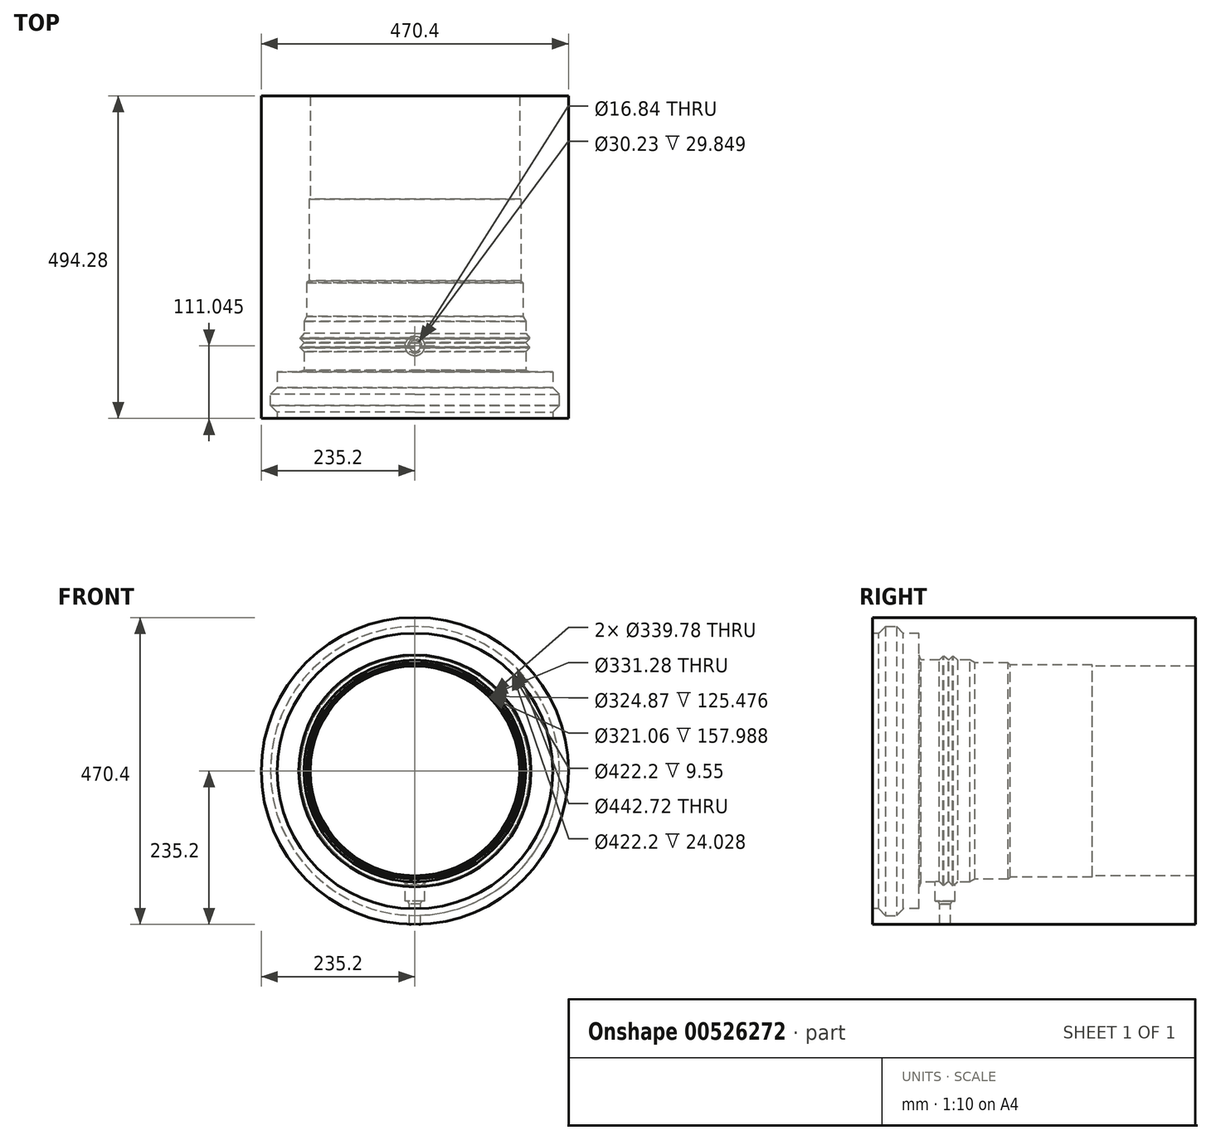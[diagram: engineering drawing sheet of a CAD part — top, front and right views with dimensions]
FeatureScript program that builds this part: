
annotation { "Feature Type Name" : "Feature", "Feature Type Description" : "" }
export const myFeature = defineFeature(function(context is Context, id is Id, definition is map)
    precondition{}
    {
        {
            var Q0;
            Q0=qCreatedBy(makeId("Front.planeOp"),FACE);
            var sketch = newSketch(context, id + "F0", { "sketchPlane" : qUnion([Q0])});
            skCircle(sketch, "E0", {"center": v(0, 0) * mm, "radius": 235.2 * mm});
            skSolve(sketch);
        }
        {
            var Q0;
            Q0 = qSketchRegion(id + "F0", true);
            extrude(context, id + "F1", {"entities" : qUnion([Q0]), "depth" : 494.28 * mm, "offsetDistance" : 25.4 * mm});
        }
        {
            var Q0;
            Q0=makeQuery(id+"F1.opExtrude","CAP_FACE",FACE,{"disambiguationData":[OSD([sQuery(id+"F0.wireOp",EDGE,"E0")])],"isStart":false});
            var sketch = newSketch(context, id + "F2", { "sketchPlane" : qUnion([Q0])});
            skCircle(sketch, "E1", {"center": v(0, 0) * mm, "radius": 160.53 * mm});
            skSolve(sketch);
        }
        {
            var Q0;
            Q0 = qSketchRegion(id + "F2", true);
            var Q1;
            Q1=makeQuery(id+"F2.imprint","IMPRINT",FACE,{"disambiguationData":[TD([[makeQuery(id+"F2.imprint","IMPRINT",EDGE,{"derivedFrom":sQuery(id+"F2.wireOp",EDGE,"E1")}),1.0]])]});
            extrude(context, id + "F3", {"entities" : qUnion([Q0, Q1]), "operationType" : NewBodyOperationType.REMOVE, "oppositeDirection" : true, "depth" : 947.42 * mm, "offsetDistance" : 25.4 * mm});
        }
        {
            var Q0;
            Q0=makeQuery(id+"F1.opExtrude","CAP_FACE",FACE,{"disambiguationData":[OSD([sQuery(id+"F0.wireOp",EDGE,"E0")])],"isStart":false});
            var sketch = newSketch(context, id + "F4", { "sketchPlane" : qUnion([Q0])});
            skCircle(sketch, "E2", {"center": v(0, 0) * mm, "radius": 162.43 * mm});
            skCircle(sketch, "E3", {"center": v(0, 0) * mm, "radius": 139.01 * mm});
            skSolve(sketch);
        }
        {
            var Q0;
            Q0 = qSketchRegion(id + "F4", true);
            extrude(context, id + "F5", {"entities" : qUnion([Q0]), "operationType" : NewBodyOperationType.REMOVE, "oppositeDirection" : true, "depth" : 336.3 * mm, "offsetDistance" : 25.4 * mm});
        }
        {
            var Q0;
            Q0=makeQuery(id+"F1.opExtrude","CAP_FACE",FACE,{"disambiguationData":[OSD([sQuery(id+"F0.wireOp",EDGE,"E0")])],"isStart":false});
            var sketch = newSketch(context, id + "F6", { "sketchPlane" : qUnion([Q0])});
            skCircle(sketch, "E4", {"center": v(0, 0) * mm, "radius": 165.64 * mm});
            skCircle(sketch, "E5", {"center": v(0, 0) * mm, "radius": 130.06 * mm});
            skSolve(sketch);
        }
        {
            var Q0;
            Q0 = qSketchRegion(id + "F6", true);
            extrude(context, id + "F7", {"entities" : qUnion([Q0]), "operationType" : NewBodyOperationType.REMOVE, "oppositeDirection" : true, "depth" : 205.74 * mm, "offsetDistance" : 25.4 * mm});
        }
        {
            var Q0;
            Q0=makeQuery(id+"F7.boolean.opBoolean","INTERSECT",EDGE,{"derivedFrom":[makeQuery(id+"F5.boolean.opBoolean","COPY",FACE,{"derivedFrom":makeQuery(id+"F5.opExtrude","SWEPT_FACE",FACE,{"disambiguationData":[OSD([sQuery(id+"F4.wireOp",EDGE,"E2")])]})}),makeQuery(id+"F7.opExtrude","CAP_FACE",FACE,{"disambiguationData":[OSD([sQuery(id+"F6.wireOp",EDGE,"E4"),sQuery(id+"F6.wireOp",EDGE,"E5")])],"isStart":false})]});
            chamfer(context, id + "F8", {"entities" : qUnion([Q0]), "width" : 5.08 * mm, "tangentPropagation" : true});
        }
        {
            var Q0;
            Q0=makeQuery(id+"F1.opExtrude","CAP_FACE",FACE,{"disambiguationData":[OSD([sQuery(id+"F0.wireOp",EDGE,"E0")])],"isStart":false});
            var sketch = newSketch(context, id + "F9", { "sketchPlane" : qUnion([Q0])});
            skCircle(sketch, "E6", {"center": v(0, 0) * mm, "radius": 169.89 * mm});
            skCircle(sketch, "E7", {"center": v(0, 0) * mm, "radius": 9.4 * mm});
            skSolve(sketch);
        }
        {
            var Q0;
            Q0 = qSketchRegion(id + "F9", true);
            extrude(context, id + "F10", {"entities" : qUnion([Q0]), "operationType" : NewBodyOperationType.REMOVE, "oppositeDirection" : true, "depth" : 147.57 * mm, "offsetDistance" : 25.4 * mm});
        }
        {
            var Q0;
            Q0=makeQuery(id+"F10.boolean.opBoolean","INTERSECT",EDGE,{"derivedFrom":[makeQuery(id+"F7.boolean.opBoolean","COPY",FACE,{"derivedFrom":makeQuery(id+"F7.opExtrude","SWEPT_FACE",FACE,{"disambiguationData":[OSD([sQuery(id+"F6.wireOp",EDGE,"E4")])]})}),makeQuery(id+"F10.opExtrude","CAP_FACE",FACE,{"disambiguationData":[OSD([sQuery(id+"F9.wireOp",EDGE,"E6"),sQuery(id+"F9.wireOp",EDGE,"E7")])],"isStart":false})]});
            chamfer(context, id + "F11", {"entities" : qUnion([Q0]), "chamferType" : ChamferType.OFFSET_ANGLE, "width" : 5.08 * mm, "oppositeDirection" : false, "angle" : 60 * degree, "tangentPropagation" : true});
        }
        {
            var Q0;
            Q0=makeQuery(id+"F1.opExtrude","CAP_FACE",FACE,{"disambiguationData":[OSD([sQuery(id+"F0.wireOp",EDGE,"E0")])],"isStart":false});
            var sketch = newSketch(context, id + "F12", { "sketchPlane" : qUnion([Q0])});
            skCircle(sketch, "E8", {"center": v(0, 0) * mm, "radius": 211.1 * mm});
            skCircle(sketch, "E9", {"center": v(0, 0) * mm, "radius": 37.7 * mm});
            skSolve(sketch);
        }
        {
            var Q0;
            Q0 = qSketchRegion(id + "F12", true);
            extrude(context, id + "F13", {"entities" : qUnion([Q0]), "operationType" : NewBodyOperationType.REMOVE, "oppositeDirection" : true, "depth" : 71.12 * mm, "offsetDistance" : 25.4 * mm});
        }
        {
            var Q0;
            Q0=qCreatedBy(makeId("Right.planeOp"),FACE);
            var sketch = newSketch(context, id + "F14", { "sketchPlane" : qUnion([Q0])});
            skPoint(sketch, "E10", {"position": v(-423.16, -177.8) * mm});
            skLineSegment(sketch, "E11", {"start": v(0, 0) * mm, "end": v(-511.48, 0) * mm});
            skLineSegment(sketch, "E12", {"start": v(-423.16, -177.8) * mm, "end": v(-415.34, -156.3) * mm});
            skLineSegment(sketch, "E13", {"start": v(-415.34, -156.3) * mm, "end": v(-438.26, -160.36) * mm});
            skLineSegment(sketch, "E14", {"start": v(-438.26, -160.36) * mm, "end": v(-423.16, -177.8) * mm});
            skPoint(sketch, "E15", {"position": v(-474.47, -221.36) * mm});
            skLineSegment(sketch, "E16", {"start": v(-474.47, -221.36) * mm, "end": v(-457.45, -221.36) * mm});
            skLineSegment(sketch, "E17", {"start": v(-457.45, -221.36) * mm, "end": v(-444.69, -208.6) * mm});
            skLineSegment(sketch, "E18", {"start": v(-474.47, -221.36) * mm, "end": v(-489.41, -206.42) * mm});
            skLineSegment(sketch, "E19", {"start": v(-489.41, -206.42) * mm, "end": v(-444.69, -208.6) * mm});
            skSolve(sketch);
        }
        {
            var Q0;
            Q0 = qSketchRegion(id + "F14", true);
            var Q1;
            Q1=sQuery(id+"F14.wireOp",EDGE,"E11");
            revolve(context, id + "F15", {"operationType" : NewBodyOperationType.REMOVE, "entities" : qUnion([Q0]), "axis" : qUnion([Q1]), "revolveType" : RevolveType.FULL});
        }
        {
            var Q0;
            Q0=qCreatedBy(makeId("Top.planeOp"),FACE);
            var sketch = newSketch(context, id + "F16", { "sketchPlane" : qUnion([Q0])});
            skLineSegment(sketch, "E20", {"start": v(0, -501.61) * mm, "end": v(0, -486.78) * mm});
            skPoint(sketch, "E21", {"position": v(169.89, -392.1) * mm});
            skLineSegment(sketch, "E22", {"start": v(175.64, -386.35) * mm, "end": v(175.64, -385.14) * mm});
            skLineSegment(sketch, "E23", {"start": v(169.89, -392.1) * mm, "end": v(175.64, -386.35) * mm});
            skLineSegment(sketch, "E24", {"start": v(169.89, -378.28) * mm, "end": v(169.89, -377.77) * mm});
            skLineSegment(sketch, "E25", {"start": v(169.89, -377.77) * mm, "end": v(175.64, -372.02) * mm});
            skPoint(sketch, "E26", {"position": v(169.89, -378.28) * mm});
            skLineSegment(sketch, "E27", {"start": v(169.89, -378.28) * mm, "end": v(175.7, -385.2) * mm});
            skLineSegment(sketch, "E28.trimOffspring", {"start": v(175.64, -372.02) * mm, "end": v(175.64, -370.84) * mm});
            skPoint(sketch, "E29.start.orphan", {"position": v(169.89, -362.9) * mm});
            skLineSegment(sketch, "E30", {"start": v(169.89, -363.98) * mm, "end": v(175.64, -370.84) * mm});
            skLineSegment(sketch, "E31", {"start": v(169.89, -392.1) * mm, "end": v(164, -392.1) * mm});
            skLineSegment(sketch, "E32", {"start": v(164, -392.1) * mm, "end": v(164, -363.98) * mm});
            skLineSegment(sketch, "E33", {"start": v(164, -363.98) * mm, "end": v(169.89, -363.98) * mm});
            skSolve(sketch);
        }
        {
            var Q0;
            Q0 = qSketchRegion(id + "F16", true);
            var Q1;
            Q1=sQuery(id+"F16.wireOp",EDGE,"E20");
            revolve(context, id + "F17", {"operationType" : NewBodyOperationType.REMOVE, "entities" : qUnion([Q0]), "axis" : qUnion([Q1]), "revolveType" : RevolveType.FULL, "oppositeDirection" : true});
        }
        {
            var Q0;
            Q0=qCreatedBy(makeId("Top.planeOp"),FACE);
            cPlane(context, id + "F18", {"entities" : qUnion([Q0]), "cplaneType" : CPlaneType.OFFSET, "offset" : 164.6 * mm, "oppositeDirection" : true, "width" : 152.4 * mm, "height" : 152.4 * mm});
        }
        {
            var Q0;
            Q0=qCreatedBy(id+"F18.planeOp",FACE);
            var sketch = newSketch(context, id + "F19", { "sketchPlane" : qUnion([Q0])});
            skCircle(sketch, "E34", {"center": v(0, -383.24) * mm, "radius": 8.42 * mm});
            skSolve(sketch);
        }
        {
            var Q0;
            Q0 = qSketchRegion(id + "F19", true);
            extrude(context, id + "F20", {"entities" : qUnion([Q0]), "operationType" : NewBodyOperationType.REMOVE, "oppositeDirection" : true, "depth" : 76.2 * mm, "offsetDistance" : 25.4 * mm});
        }
        {
            var Q0;
            Q0=qCreatedBy(id+"F18.planeOp",FACE);
            var sketch = newSketch(context, id + "F21", { "sketchPlane" : qUnion([Q0])});
            skCircle(sketch, "E35", {"center": v(0, -383.24) * mm, "radius": 15.11 * mm});
            skSolve(sketch);
        }
        {
            var Q0;
            Q0 = qSketchRegion(id + "F21", true);
            extrude(context, id + "F22", {"entities" : qUnion([Q0]), "operationType" : NewBodyOperationType.REMOVE, "oppositeDirection" : true, "depth" : 34.54 * mm, "offsetDistance" : 25.4 * mm});
        }
        {
            var Q0;
            Q0=makeQuery(id+"F22.boolean.opBoolean","INTERSECT",EDGE,{"derivedFrom":[makeQuery(id+"F20.boolean.opBoolean","COPY",FACE,{"derivedFrom":makeQuery(id+"F20.opExtrude","SWEPT_FACE",FACE,{"disambiguationData":[OSD([sQuery(id+"F19.wireOp",EDGE,"E34")])]})}),makeQuery(id+"F22.opExtrude","CAP_FACE",FACE,{"disambiguationData":[OSD([sQuery(id+"F21.wireOp",EDGE,"E35")])],"isStart":false})]});
            chamfer(context, id + "F23", {"entities" : qUnion([Q0]), "chamferType" : ChamferType.OFFSET_ANGLE, "width" : 2.54 * mm, "oppositeDirection" : false, "angle" : 60 * degree, "tangentPropagation" : true});
        }
    });
